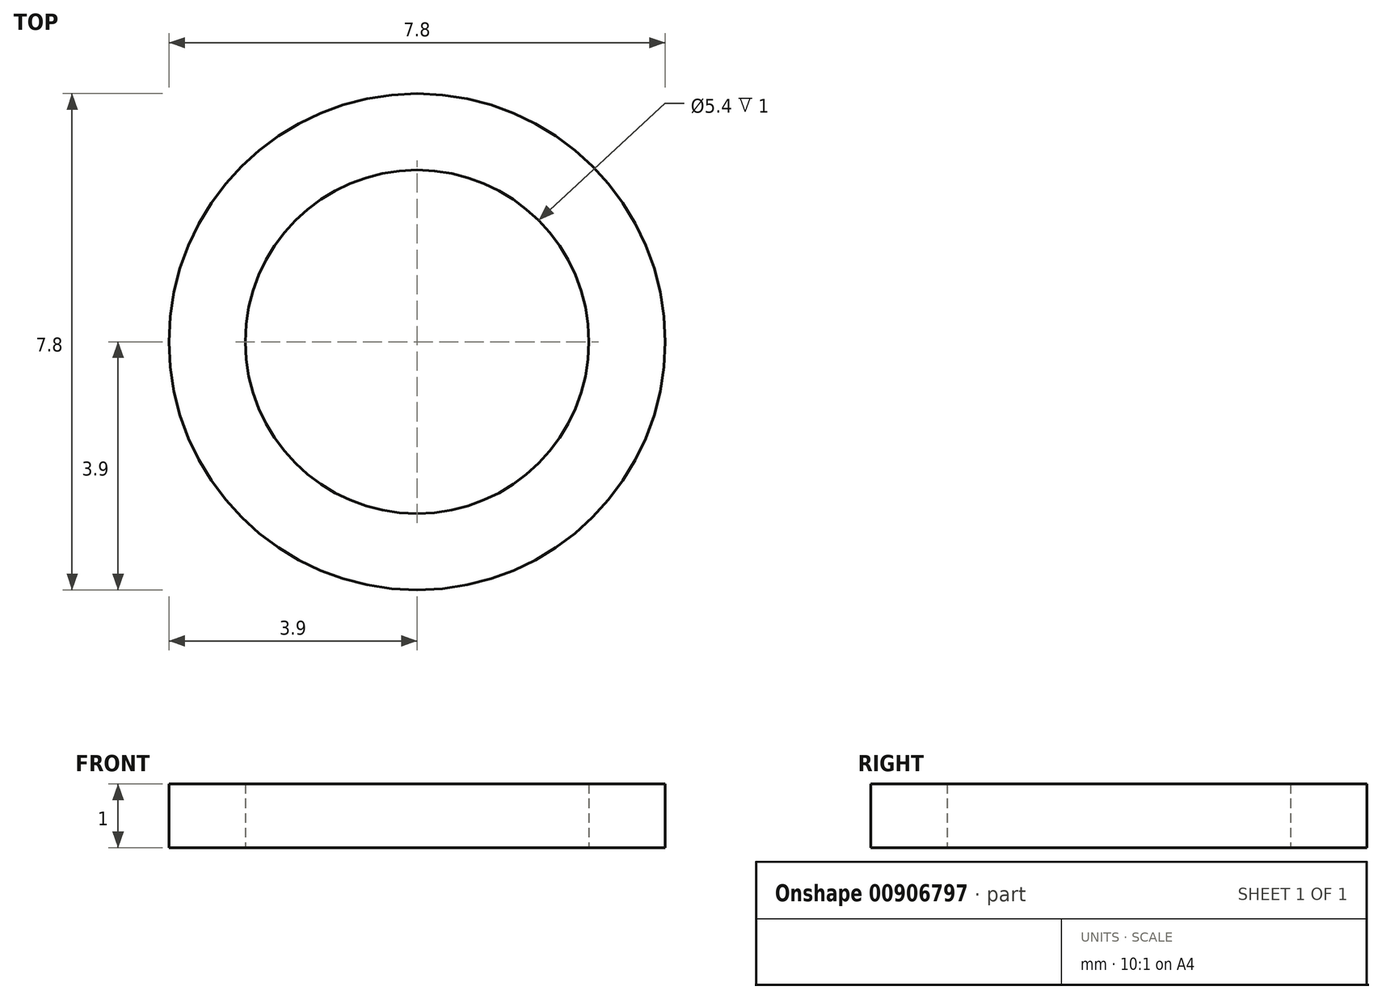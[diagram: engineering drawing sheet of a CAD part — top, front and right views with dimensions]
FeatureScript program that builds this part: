
annotation { "Feature Type Name" : "Feature", "Feature Type Description" : "" }
export const myFeature = defineFeature(function(context is Context, id is Id, definition is map)
    precondition{}
    {
        {
            var Q0;
            Q0=qCreatedBy(makeId("Top.planeOp"),FACE);
            var sketch = newSketch(context, id + "F0", { "sketchPlane" : qUnion([Q0])});
            skCircle(sketch, "E0", {"center": v(0, 0) * mm, "radius": 3.9 * mm});
            skCircle(sketch, "E1", {"center": v(0, 0) * mm, "radius": 2.7 * mm});
            skSolve(sketch);
        }
        {
            var Q0;
            Q0=makeQuery(id+"F0.imprint","IMPRINT",FACE,{"disambiguationData":[TD([[makeQuery(id+"F0.imprint","IMPRINT",EDGE,{"derivedFrom":sQuery(id+"F0.wireOp",EDGE,"E0")}),1.0]])]});
            extrude(context, id + "F1", {"entities" : qUnion([Q0]), "depth" : 1 * mm, "offsetDistance" : 25 * mm});
        }
    });
